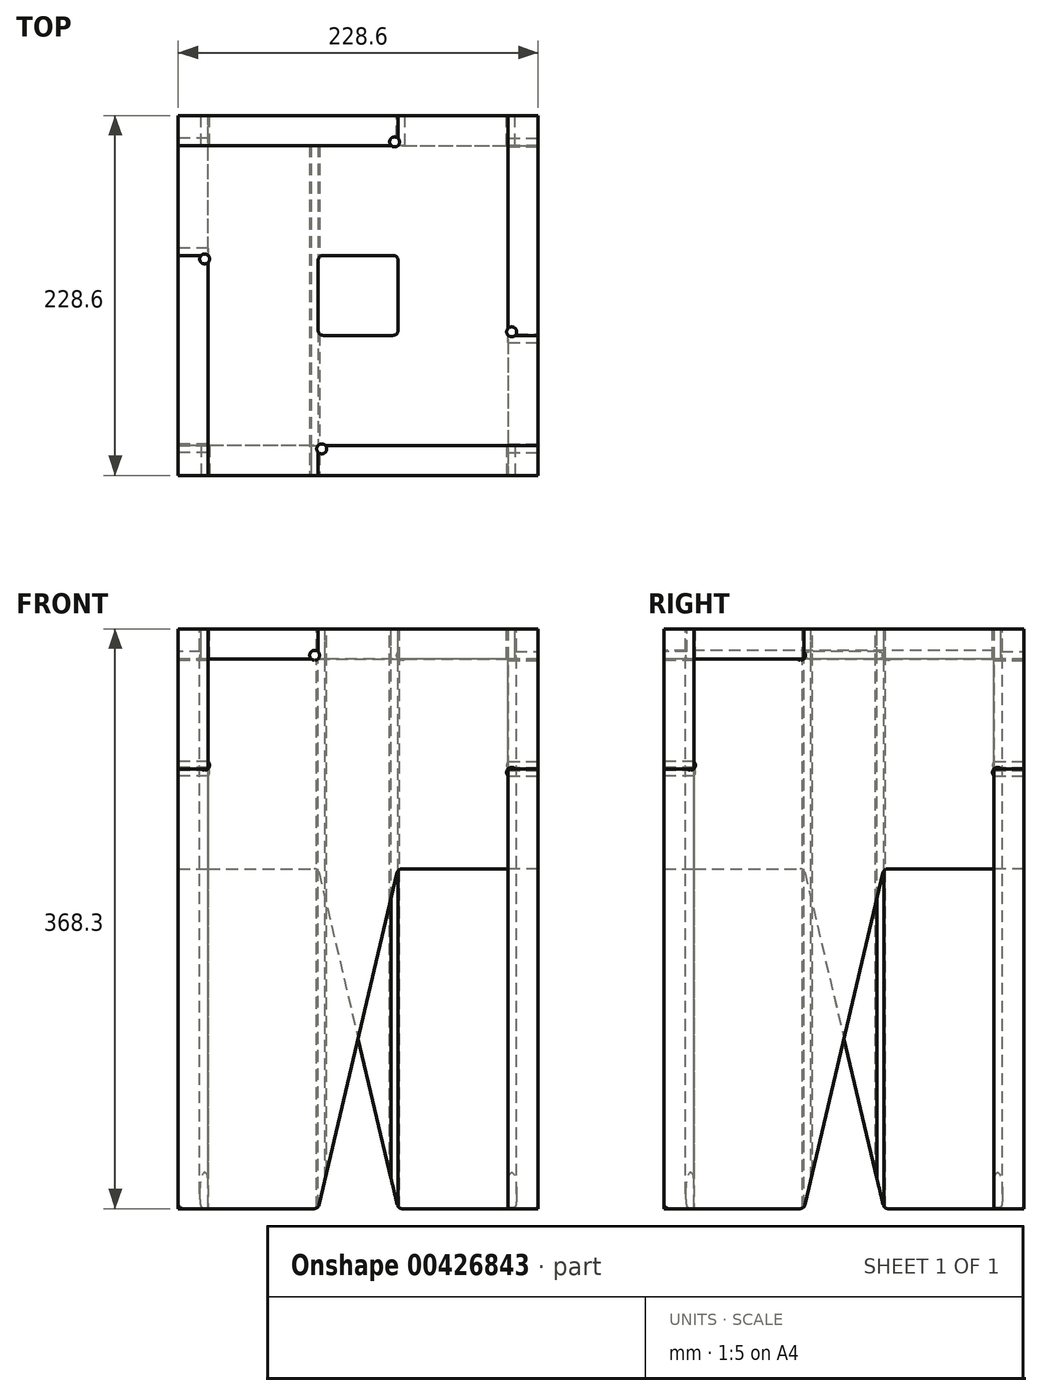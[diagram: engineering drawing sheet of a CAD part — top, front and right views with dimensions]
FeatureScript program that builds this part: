
annotation { "Feature Type Name" : "Feature", "Feature Type Description" : "" }
export const myFeature = defineFeature(function(context is Context, id is Id, definition is map)
    precondition{}
    {
        {
            var Q0;
            Q0=qCreatedBy(makeId("Top.planeOp"),FACE);
            var sketch = newSketch(context, id + "F0", { "sketchPlane" : qUnion([Q0])});
            skLineSegment(sketch, "E0.bottom", {"start": v(114.3, 114.3) * mm, "end": v(-114.3, 114.3) * mm});
            skLineSegment(sketch, "E0.top", {"start": v(114.3, -114.3) * mm, "end": v(-114.3, -114.3) * mm});
            skLineSegment(sketch, "E0.left", {"start": v(114.3, 114.3) * mm, "end": v(114.3, -114.3) * mm});
            skLineSegment(sketch, "E0.right", {"start": v(-114.3, 114.3) * mm, "end": v(-114.3, -114.3) * mm});
            skPoint(sketch, "E0.middle", {"position": v(0, 0) * mm});
            skLineSegment(sketch, "E1.bottom", {"start": v(25.4, 25.4) * mm, "end": v(-25.4, 25.4) * mm});
            skLineSegment(sketch, "E1.top", {"start": v(25.4, -25.4) * mm, "end": v(-25.4, -25.4) * mm});
            skLineSegment(sketch, "E1.left", {"start": v(25.4, 25.4) * mm, "end": v(25.4, -25.4) * mm});
            skLineSegment(sketch, "E1.right", {"start": v(-25.4, 25.4) * mm, "end": v(-25.4, -25.4) * mm});
            skSolve(sketch);
        }
        {
            var Q0;
            Q0 = qSketchRegion(id + "F0", true);
            extrude(context, id + "F1", {"entities" : qUnion([Q0]), "oppositeDirection" : true, "depth" : 19.05 * mm});
        }
        {
            var Q0;
            Q0=makeQuery(id+"F1.opExtrude","CAP_FACE",FACE,{"disambiguationData":[OSD([sQuery(id+"F0.wireOp",EDGE,"E0.bottom"),sQuery(id+"F0.wireOp",EDGE,"E0.top"),sQuery(id+"F0.wireOp",EDGE,"E0.left"),sQuery(id+"F0.wireOp",EDGE,"E0.right")])],"isStart":true});
            var sketch = newSketch(context, id + "F2", { "sketchPlane" : qUnion([Q0])});
            skLineSegment(sketch, "E2.bottom", {"start": v(-114.3, 114.3) * mm, "end": v(25.4, 114.3) * mm});
            skLineSegment(sketch, "E2.top", {"start": v(-114.3, 95.25) * mm, "end": v(25.4, 95.25) * mm});
            skLineSegment(sketch, "E2.left", {"start": v(-114.3, 114.3) * mm, "end": v(-114.3, 95.25) * mm});
            skLineSegment(sketch, "E2.right", {"start": v(25.4, 114.3) * mm, "end": v(25.4, 95.25) * mm});
            skLineSegment(sketch, "E3.1.0", {"start": v(-125.19, -1569.44) * mm, "end": v(-125.19, -1429.74) * mm});
            skLineSegment(sketch, "E3.1.1", {"start": v(-106.14, -1569.44) * mm, "end": v(-106.14, -1429.74) * mm});
            skLineSegment(sketch, "E3.1.2", {"start": v(-125.19, -1569.44) * mm, "end": v(-106.14, -1569.44) * mm});
            skLineSegment(sketch, "E3.1.3", {"start": v(-125.19, -1429.74) * mm, "end": v(-106.14, -1429.74) * mm});
            skLineSegment(sketch, "E3.2.0", {"start": v(1558.55, -1580.32) * mm, "end": v(1418.85, -1580.32) * mm});
            skLineSegment(sketch, "E3.2.1", {"start": v(1558.55, -1561.27) * mm, "end": v(1418.85, -1561.27) * mm});
            skLineSegment(sketch, "E3.2.2", {"start": v(1558.55, -1580.32) * mm, "end": v(1558.55, -1561.27) * mm});
            skLineSegment(sketch, "E3.2.3", {"start": v(1418.85, -1580.32) * mm, "end": v(1418.85, -1561.27) * mm});
            skLineSegment(sketch, "E3.3.0", {"start": v(1569.44, 103.41) * mm, "end": v(1569.44, -36.29) * mm});
            skLineSegment(sketch, "E3.3.1", {"start": v(1550.39, 103.41) * mm, "end": v(1550.39, -36.29) * mm});
            skLineSegment(sketch, "E3.3.2", {"start": v(1569.44, 103.41) * mm, "end": v(1550.39, 103.41) * mm});
            skLineSegment(sketch, "E3.3.3", {"start": v(1569.44, -36.29) * mm, "end": v(1550.39, -36.29) * mm});
            skPoint(sketch, "E3.center", {"position": v(722.13, -733.01) * mm});
            skLineSegment(sketch, "E4.1.0", {"start": v(-114.3, -114.3) * mm, "end": v(-114.3, 25.4) * mm});
            skLineSegment(sketch, "E4.1.1", {"start": v(-95.25, -114.3) * mm, "end": v(-95.25, 25.4) * mm});
            skLineSegment(sketch, "E4.1.2", {"start": v(-114.3, -114.3) * mm, "end": v(-95.25, -114.3) * mm});
            skLineSegment(sketch, "E4.1.3", {"start": v(-114.3, 25.4) * mm, "end": v(-95.25, 25.4) * mm});
            skLineSegment(sketch, "E4.2.0", {"start": v(114.3, -114.3) * mm, "end": v(-25.4, -114.3) * mm});
            skLineSegment(sketch, "E4.2.1", {"start": v(114.3, -95.25) * mm, "end": v(-25.4, -95.25) * mm});
            skLineSegment(sketch, "E4.2.2", {"start": v(114.3, -114.3) * mm, "end": v(114.3, -95.25) * mm});
            skLineSegment(sketch, "E4.2.3", {"start": v(-25.4, -114.3) * mm, "end": v(-25.4, -95.25) * mm});
            skLineSegment(sketch, "E4.3.0", {"start": v(114.3, 114.3) * mm, "end": v(114.3, -25.4) * mm});
            skLineSegment(sketch, "E4.3.1", {"start": v(95.25, 114.3) * mm, "end": v(95.25, -25.4) * mm});
            skLineSegment(sketch, "E4.3.2", {"start": v(114.3, 114.3) * mm, "end": v(95.25, 114.3) * mm});
            skLineSegment(sketch, "E4.3.3", {"start": v(114.3, -25.4) * mm, "end": v(95.25, -25.4) * mm});
            skPoint(sketch, "E4.center", {"position": v(0, 0) * mm});
            skSolve(sketch);
        }
        {
            var Q0;
            Q0 = qSketchRegion(id + "F2", true);
            extrude(context, id + "F3", {"entities" : qUnion([Q0]), "operationType" : NewBodyOperationType.REMOVE, "endBound" : BoundingType.THROUGH_ALL, "oppositeDirection" : true, "depth" : 25.4 * mm});
        }
        {
            var Q0;
            Q0=makeQuery(id+"F3.boolean.opBoolean","COPY",FACE,{"derivedFrom":makeQuery(id+"F3.opExtrude","SWEPT_FACE",FACE,{"disambiguationData":[OSD([sQuery(id+"F2.wireOp",EDGE,"E4.2.1")])]})});
            var sketch = newSketch(context, id + "F4", { "sketchPlane" : qUnion([Q0])});
            skLineSegment(sketch, "E5", {"start": v(-25.4, -19.05) * mm, "end": v(-95.25, -19.05) * mm});
            skLineSegment(sketch, "E6", {"start": v(-25.4, -19.05) * mm, "end": v(-25.4, 0) * mm});
            skLineSegment(sketch, "E7", {"start": v(-25.4, 0) * mm, "end": v(114.3, 0) * mm});
            skLineSegment(sketch, "E8", {"start": v(-25.4, -368.3) * mm, "end": v(-114.3, -368.3) * mm});
            skLineSegment(sketch, "E9", {"start": v(25.4, -152.4) * mm, "end": v(-25.4, -368.3) * mm});
            skLineSegment(sketch, "E10", {"start": v(-95.25, -88.9) * mm, "end": v(-95.25, -19.05) * mm});
            skLineSegment(sketch, "E11", {"start": v(114.3, 0) * mm, "end": v(114.3, -88.9) * mm});
            skLineSegment(sketch, "E12", {"start": v(-95.25, -88.9) * mm, "end": v(-114.3, -88.9) * mm});
            skLineSegment(sketch, "E13", {"start": v(-114.3, -88.9) * mm, "end": v(-114.3, -368.3) * mm});
            skLineSegment(sketch, "E14", {"start": v(114.3, -88.9) * mm, "end": v(95.25, -88.9) * mm});
            skLineSegment(sketch, "E15", {"start": v(95.25, -88.9) * mm, "end": v(95.25, -152.4) * mm});
            skLineSegment(sketch, "E16", {"start": v(95.25, -152.4) * mm, "end": v(25.4, -152.4) * mm});
            skSolve(sketch);
        }
        {
            var Q0;
            Q0 = qSketchRegion(id + "F4", true);
            extrude(context, id + "F5", {"entities" : qUnion([Q0]), "depth" : 19.05 * mm});
        }
        {
            var Q0;
            Q0=qCreatedBy(makeId("Front.planeOp"),FACE);
            var sketch = newSketch(context, id + "F6", { "sketchPlane" : qUnion([Q0])});
            skLineSegment(sketch, "E17", {"start": v(0, 0) * mm, "end": v(0, 173.39) * mm, "construction": true});
            skSolve(sketch);
        }
        {
            var Q0;
            Q0=makeQuery(id+"F5.opExtrude","SWEPT_EDGE",EDGE,{"disambiguationData":[OSD([sQuery(id+"F4.wireOp",EDGE,"E8"),sQuery(id+"F4.wireOp",EDGE,"E9")])]});
            var Q1;
            Q1=makeQuery(id+"F5.opExtrude","SWEPT_EDGE",EDGE,{"disambiguationData":[OSD([sQuery(id+"F4.wireOp",EDGE,"E8"),sQuery(id+"F4.wireOp",EDGE,"E13")])]});
            var Q2;
            Q2=makeQuery(id+"F1.opExtrude","SWEPT_EDGE",EDGE,{"disambiguationData":[OSD([sQuery(id+"F0.wireOp",EDGE,"E1.bottom"),sQuery(id+"F0.wireOp",EDGE,"E1.left")])]});
            var Q3;
            Q3=makeQuery(id+"F1.opExtrude","SWEPT_EDGE",EDGE,{"disambiguationData":[OSD([sQuery(id+"F0.wireOp",EDGE,"E1.bottom"),sQuery(id+"F0.wireOp",EDGE,"E1.right")])]});
            var Q4;
            Q4=makeQuery(id+"F1.opExtrude","SWEPT_EDGE",EDGE,{"disambiguationData":[OSD([sQuery(id+"F0.wireOp",EDGE,"E1.top"),sQuery(id+"F0.wireOp",EDGE,"E1.right")])]});
            var Q5;
            Q5=makeQuery(id+"F1.opExtrude","SWEPT_EDGE",EDGE,{"disambiguationData":[OSD([sQuery(id+"F0.wireOp",EDGE,"E1.top"),sQuery(id+"F0.wireOp",EDGE,"E1.left")])]});
            var Q6;
            Q6=makeQuery(id+"F5.opExtrude","SWEPT_EDGE",EDGE,{"disambiguationData":[OSD([sQuery(id+"F4.wireOp",EDGE,"E9"),sQuery(id+"F4.wireOp",EDGE,"E16")])]});
            fillet(context, id + "F7", {"entities" : qUnion([Q0, Q1, Q2, Q3, Q4, Q5, Q6]), "radius" : 3.17 * mm, "tangentPropagation" : true, "allowEdgeOverflow" : false});
        }
        {
            var Q0;
            Q0=makeQuery(id+"F1.opExtrude","CAP_FACE",FACE,{"disambiguationData":[OSD([sQuery(id+"F0.wireOp",EDGE,"E0.bottom"),sQuery(id+"F0.wireOp",EDGE,"E0.top"),sQuery(id+"F0.wireOp",EDGE,"E0.left"),sQuery(id+"F0.wireOp",EDGE,"E0.right"),sQuery(id+"F0.wireOp",EDGE,"E1.bottom"),sQuery(id+"F0.wireOp",EDGE,"E1.top"),sQuery(id+"F0.wireOp",EDGE,"E1.left"),sQuery(id+"F0.wireOp",EDGE,"E1.right")])],"isStart":true});
            var sketch = newSketch(context, id + "F8", { "sketchPlane" : qUnion([Q0])});
            skCircle(sketch, "E18", {"center": v(23.15, 97.5) * mm, "radius": 3.18 * mm});
            skLineSegment(sketch, "E19", {"start": v(23.15, 97.5) * mm, "end": v(25.4, 95.25) * mm, "construction": true});
            skCircle(sketch, "E20.1.0", {"center": v(-97.5, 23.15) * mm, "radius": 3.18 * mm});
            skCircle(sketch, "E20.2.0", {"center": v(-23.15, -97.5) * mm, "radius": 3.18 * mm});
            skCircle(sketch, "E20.3.0", {"center": v(97.5, -23.15) * mm, "radius": 3.18 * mm});
            skPoint(sketch, "E20.center", {"position": v(0, 0) * mm});
            skSolve(sketch);
        }
        {
            var Q0;
            Q0 = qSketchRegion(id + "F8", true);
            extrude(context, id + "F9", {"entities" : qUnion([Q0]), "operationType" : NewBodyOperationType.REMOVE, "endBound" : BoundingType.THROUGH_ALL, "oppositeDirection" : true, "depth" : 25.4 * mm});
        }
        {
            var Q0;
            Q0=makeQuery(id+"F5.opExtrude","CAP_FACE",FACE,{"disambiguationData":[OSD([sQuery(id+"F4.wireOp",EDGE,"E5"),sQuery(id+"F4.wireOp",EDGE,"E6"),sQuery(id+"F4.wireOp",EDGE,"E7"),sQuery(id+"F4.wireOp",EDGE,"E8"),sQuery(id+"F4.wireOp",EDGE,"E9"),sQuery(id+"F4.wireOp",EDGE,"E10"),sQuery(id+"F4.wireOp",EDGE,"E11"),sQuery(id+"F4.wireOp",EDGE,"E12"),sQuery(id+"F4.wireOp",EDGE,"E13"),sQuery(id+"F4.wireOp",EDGE,"E14"),sQuery(id+"F4.wireOp",EDGE,"E15"),sQuery(id+"F4.wireOp",EDGE,"E16")])],"isStart":false});
            var sketch = newSketch(context, id + "F10", { "sketchPlane" : qUnion([Q0])});
            skCircle(sketch, "E21", {"center": v(-27.65, -16.8) * mm, "radius": 3.17 * mm});
            skCircle(sketch, "E22", {"center": v(-97.5, -86.65) * mm, "radius": 3.17 * mm});
            skCircle(sketch, "E23", {"center": v(97.5, -91.15) * mm, "radius": 3.17 * mm});
            skLineSegment(sketch, "E24", {"start": v(-27.65, -16.8) * mm, "end": v(-25.4, -19.05) * mm, "construction": true});
            skLineSegment(sketch, "E25", {"start": v(-97.5, -86.65) * mm, "end": v(-95.25, -88.9) * mm, "construction": true});
            skLineSegment(sketch, "E26", {"start": v(97.5, -91.15) * mm, "end": v(95.25, -88.9) * mm, "construction": true});
            skSolve(sketch);
        }
        {
            var Q0;
            Q0 = qSketchRegion(id + "F10", true);
            extrude(context, id + "F11", {"entities" : qUnion([Q0]), "operationType" : NewBodyOperationType.REMOVE, "endBound" : BoundingType.THROUGH_ALL, "oppositeDirection" : true, "depth" : 25.4 * mm});
        }
        {
            var Q0;
            Q0=makeQuery(id+"F5.opExtrude","SWEPT_BODY",BODY,{"disambiguationData":[OSD([sQuery(id+"F4.wireOp",EDGE,"E5"),sQuery(id+"F4.wireOp",EDGE,"E6"),sQuery(id+"F4.wireOp",EDGE,"E7"),sQuery(id+"F4.wireOp",EDGE,"a7vPFoch-o8J6-scZX-Oh6H-BAf8xY4ZgOvg"),sQuery(id+"F4.wireOp",EDGE,"E8"),sQuery(id+"F4.wireOp",EDGE,"UtqFKU0p-HITZ-kTEu-TjsP-fL42qMZRZGC2")])]});
            var Q1;
            Q1=sQuery(id+"F6.wireOp",EDGE,"E17");
            circularPattern(context, id + "F12", {"entities" : qUnion([Q0]), "axis" : qUnion([Q1]), "angle" : 360 * degree, "instanceCount" : 4, "equalSpace" : true});
        }
    });
